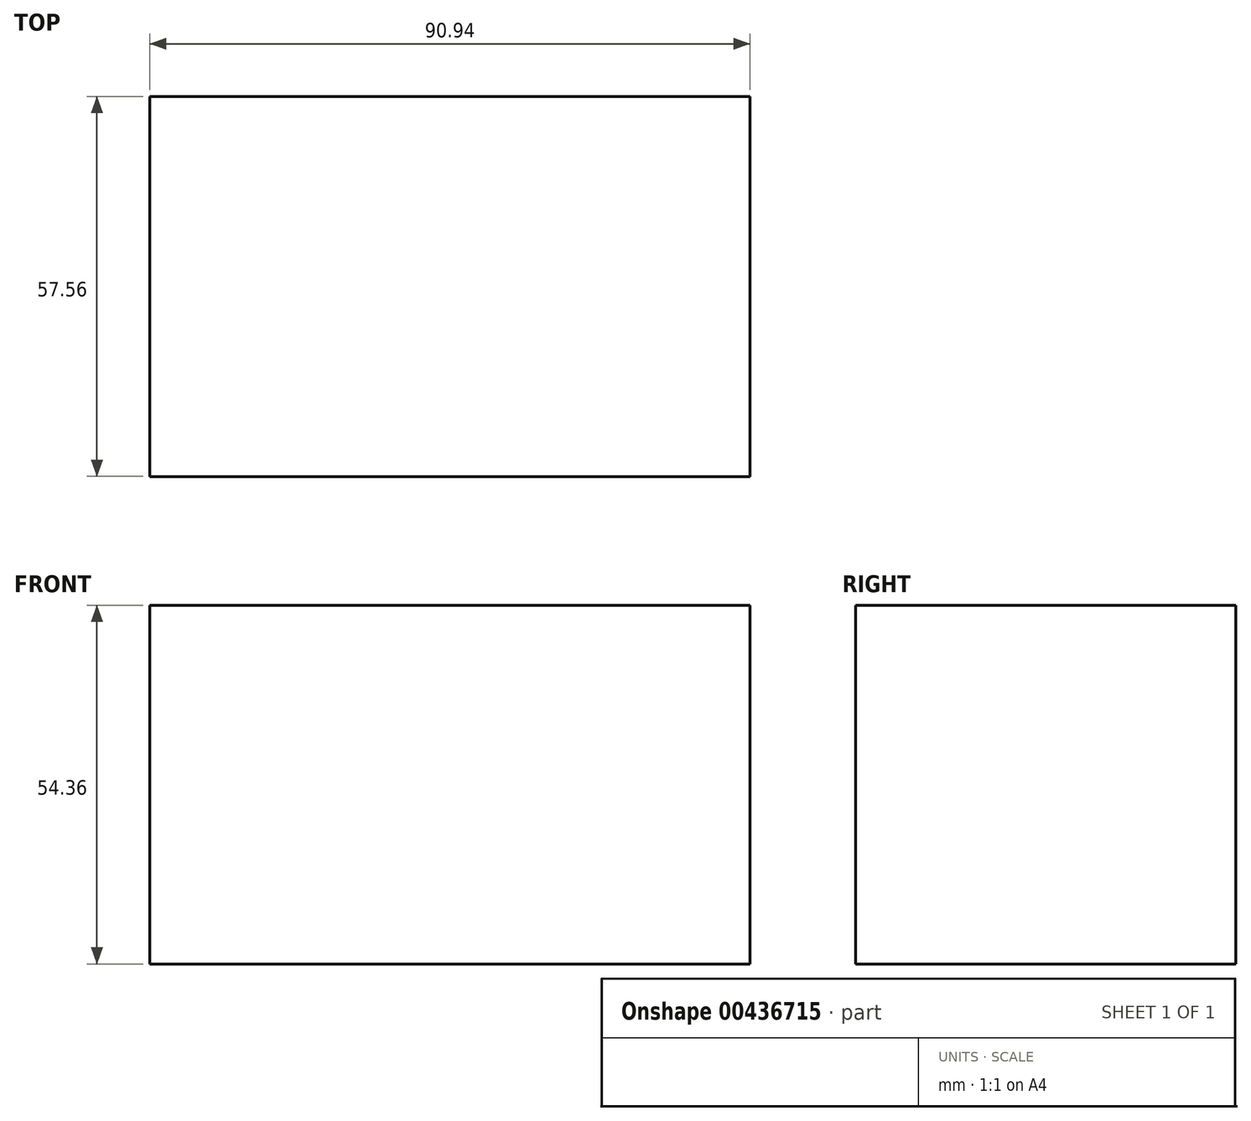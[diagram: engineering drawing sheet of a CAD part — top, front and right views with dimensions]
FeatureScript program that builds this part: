
annotation { "Feature Type Name" : "Feature", "Feature Type Description" : "" }
export const myFeature = defineFeature(function(context is Context, id is Id, definition is map)
    precondition{}
    {
        {
            var Q0;
            Q0=qCreatedBy(makeId("Top.planeOp"),FACE);
            var sketch = newSketch(context, id + "F0", { "sketchPlane" : qUnion([Q0])});
            skLineSegment(sketch, "E0.bottom", {"start": v(-53.85, 28.78) * mm, "end": v(37.1, 28.78) * mm});
            skLineSegment(sketch, "E0.top", {"start": v(-53.85, -28.78) * mm, "end": v(37.1, -28.78) * mm});
            skLineSegment(sketch, "E0.left", {"start": v(-53.85, 28.78) * mm, "end": v(-53.85, -28.78) * mm});
            skLineSegment(sketch, "E0.right", {"start": v(37.1, 28.78) * mm, "end": v(37.1, -28.78) * mm});
            skPoint(sketch, "E0.middle", {"position": v(-8.38, 0) * mm});
            skSolve(sketch);
        }
        {
            var Q0;
            Q0=makeQuery(id+"F0.imprint","IMPRINT",FACE,{"disambiguationData":[TD([[makeQuery(id+"F0.imprint","IMPRINT",EDGE,{"derivedFrom":sQuery(id+"F0.wireOp",EDGE,"E0.bottom")}),-1.0]])]});
            extrude(context, id + "F1", {"entities" : qUnion([Q0]), "depth" : 54.36 * mm, "offsetDistance" : 25.4 * mm});
        }
    });
